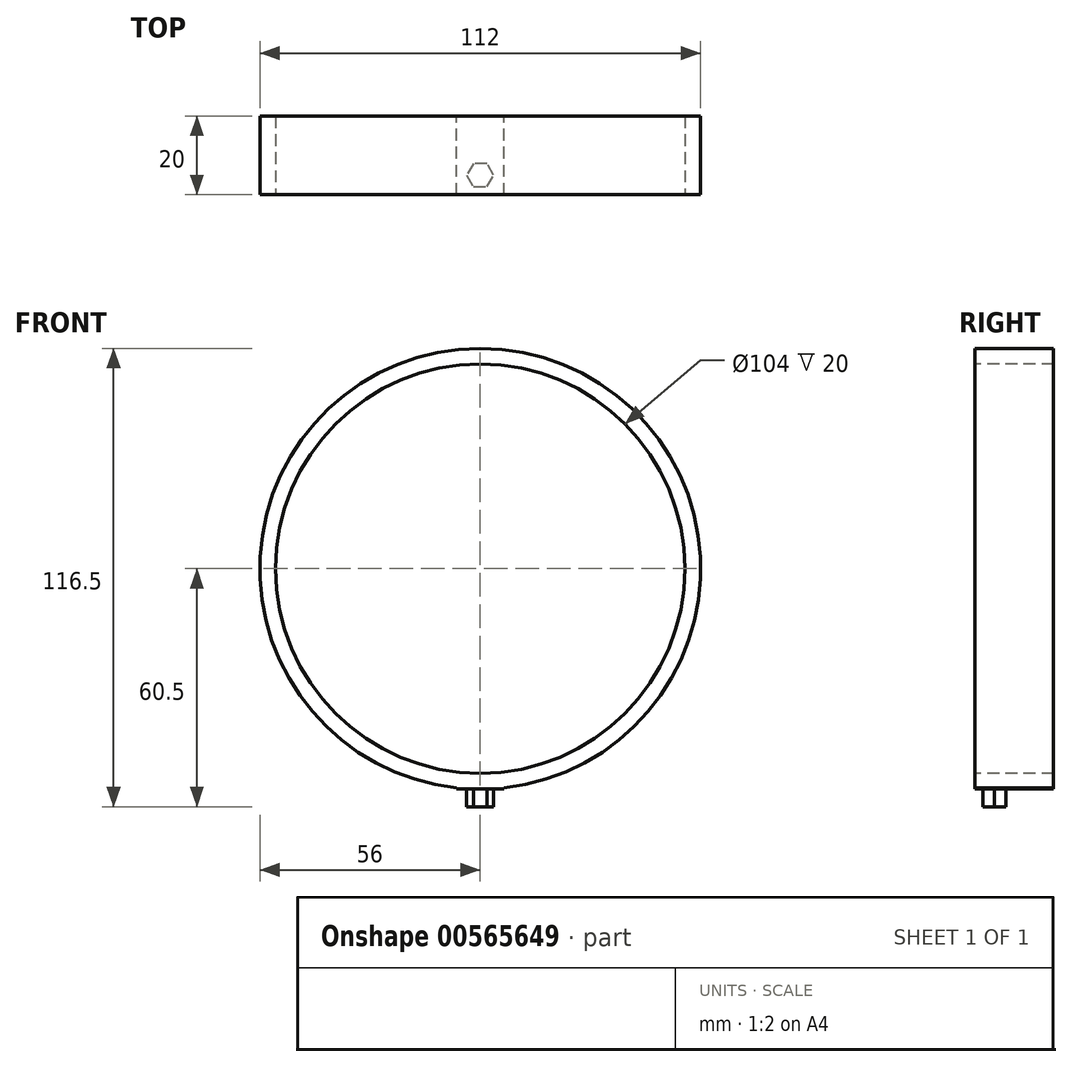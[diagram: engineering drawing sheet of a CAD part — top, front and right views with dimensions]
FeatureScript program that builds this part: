
annotation { "Feature Type Name" : "Feature", "Feature Type Description" : "" }
export const myFeature = defineFeature(function(context is Context, id is Id, definition is map)
    precondition{}
    {
        {
            var Q0;
            Q0=qCreatedBy(makeId("Front.planeOp"),FACE);
            var sketch = newSketch(context, id + "F0", { "sketchPlane" : qUnion([Q0])});
            skCircle(sketch, "E0", {"center": v(0, 0) * mm, "radius": 52 * mm});
            skCircle(sketch, "E1.0", {"center": v(0, 0) * mm, "radius": 56 * mm});
            skLineSegment(sketch, "E2.bottom", {"start": v(6, -52) * mm, "end": v(-6, -52) * mm});
            skLineSegment(sketch, "E2.top", {"start": v(6, -56) * mm, "end": v(-6, -56) * mm});
            skLineSegment(sketch, "E2.left", {"start": v(6, -52) * mm, "end": v(6, -56) * mm});
            skLineSegment(sketch, "E2.right", {"start": v(-6, -52) * mm, "end": v(-6, -56) * mm});
            skPoint(sketch, "E2.middle", {"position": v(0, -54) * mm});
            skSolve(sketch);
        }
        {
            var Q0;
            Q0=makeQuery(id+"F0.imprint","IMPRINT",FACE,{"disambiguationData":[TD([[makeQuery(id+"F0.imprint","IMPRINT",EDGE,{"derivedFrom":sQuery(id+"F0.wireOp",EDGE,"E0")}),-1.0]])]});
            var Q1;
            {var subQ6=sQuery(id+"F0.wireOp",EDGE,"E1.0");var subQ7=makeQuery(id+"F0.imprint","INTERSECT",VERTEX,{"derivedFrom":[subQ6,sQuery(id+"F0.wireOp",EDGE,"E2.top")]});Q1=makeQuery(id+"F0.imprint","IMPRINT",FACE,{"disambiguationData":[TD([[makeQuery(id+"F0.imprint","IMPRINT",EDGE,{"disambiguationData":[TD([[subQ7,1.0]])],"derivedFrom":subQ6}),1.0]])]});}
            extrude(context, id + "F1", {"entities" : qUnion([Q0, Q1]), "oppositeDirection" : true, "depth" : (60 / 4) * mm, "offsetDistance" : 25 * mm, "hasSecondDirection" : true, "secondDirectionOppositeDirection" : false, "secondDirectionDepth" : 5 * mm});
        }
        {
            var Q0;
            {var subQ5=sQuery(id+"F0.wireOp",EDGE,"E2.top");Q0=makeQuery(id+"F0.imprint","IMPRINT",FACE,{"disambiguationData":[TD([[makeQuery(id+"F0.imprint","IMPRINT",EDGE,{"derivedFrom":subQ5}),-1.0]])]});}
            var Q1;
            Q1=makeQuery(id+"F1.opExtrude","CAP_FACE",FACE,{"disambiguationData":[OSD([sQuery(id+"F0.wireOp",EDGE,"E0"),sQuery(id+"F0.wireOp",EDGE,"E1.0")])],"isStart":true});
            var Q2;
            Q2=makeQuery(id+"F1.opExtrude","CAP_FACE",FACE,{"disambiguationData":[OSD([sQuery(id+"F0.wireOp",EDGE,"E0"),sQuery(id+"F0.wireOp",EDGE,"E1.0")])],"isStart":false});
            extrude(context, id + "F2", {"entities" : qUnion([Q0]), "operationType" : NewBodyOperationType.ADD, "endBound" : BoundingType.UP_TO_SURFACE, "depth" : 15 * mm, "endBoundEntityFace" : qUnion([Q1]), "offsetDistance" : 25 * mm, "hasSecondDirection" : true, "secondDirectionBound" : SecondDirectionBoundingType.UP_TO_SURFACE, "secondDirectionOppositeDirection" : true, "secondDirectionDepth" : 25 * mm, "secondDirectionBoundEntityFace" : qUnion([Q2])});
        }
        {
            var Q0;
            {var subQ0=sQuery(id+"F0.wireOp",EDGE,"E2.top");Q0=makeQuery(id+"F2.boolean.opBoolean","MERGE",FACE,{"derivedFrom":[makeQuery(id+"F2.opExtrude","SWEPT_FACE",FACE,{"disambiguationData":[OSD([subQ0]),TDD([makeQuery(id+"F0.imprint","IMPRINT",EDGE,{"disambiguationData":[TD([[makeQuery(id+"F0.imprint","INTERSECT",VERTEX,{"derivedFrom":[subQ0,sQuery(id+"F0.wireOp",EDGE,"E2.left")]}),-1.0]])],"derivedFrom":subQ0})])]}),makeQuery(id+"F2.opExtrude","SWEPT_FACE",FACE,{"disambiguationData":[OSD([subQ0]),TDD([makeQuery(id+"F0.imprint","IMPRINT",EDGE,{"disambiguationData":[TD([[makeQuery(id+"F0.imprint","INTERSECT",VERTEX,{"derivedFrom":[subQ0,sQuery(id+"F0.wireOp",EDGE,"E2.right")]}),1.0]])],"derivedFrom":subQ0})])]})]});}
            var sketch = newSketch(context, id + "F3", { "sketchPlane" : qUnion([Q0])});
            skLineSegment(sketch, "E3", {"start": v(-6, 5) * mm, "end": v(-6, -15) * mm, "construction": true});
            skLineSegment(sketch, "E4", {"start": v(-6, -15) * mm, "end": v(6, -15) * mm, "construction": true});
            skLineSegment(sketch, "E5", {"start": v(6, -15) * mm, "end": v(6, 5) * mm, "construction": true});
            skLineSegment(sketch, "E6", {"start": v(6, 5) * mm, "end": v(-6, 5) * mm, "construction": true});
            skCircle(sketch, "E7.cCircle", {"center": v(0, 0) * mm, "radius": 3.43 * mm, "construction": true});
            skLineSegment(sketch, "E7.0", {"start": v(-3.43, 0) * mm, "end": v(-1.71, 2.97) * mm});
            skLineSegment(sketch, "E7.1", {"start": v(-1.71, 2.97) * mm, "end": v(1.71, 2.97) * mm});
            skLineSegment(sketch, "E7.2", {"start": v(1.71, 2.97) * mm, "end": v(3.43, 0) * mm});
            skLineSegment(sketch, "E7.3", {"start": v(3.43, 0) * mm, "end": v(1.71, -2.97) * mm});
            skLineSegment(sketch, "E7.4", {"start": v(1.71, -2.97) * mm, "end": v(-1.71, -2.97) * mm});
            skLineSegment(sketch, "E7.5", {"start": v(-1.71, -2.97) * mm, "end": v(-3.43, 0) * mm});
            skLineSegment(sketch, "E8", {"start": v(0, 5) * mm, "end": v(0, 0) * mm, "construction": true});
            skLineSegment(sketch, "E9", {"start": v(0, 0) * mm, "end": v(0, -15) * mm, "construction": true});
            skSolve(sketch);
        }
        {
            var Q0;
            Q0=makeQuery(id+"F3.imprint","IMPRINT",FACE,{"disambiguationData":[TD([[makeQuery(id+"F3.imprint","IMPRINT",EDGE,{"derivedFrom":sQuery(id+"F3.wireOp",EDGE,"E7.0")}),-1.0]])]});
            extrude(context, id + "F4", {"entities" : qUnion([Q0]), "operationType" : NewBodyOperationType.ADD, "depth" : 4.5 * mm, "offsetDistance" : 25 * mm});
        }
    });
